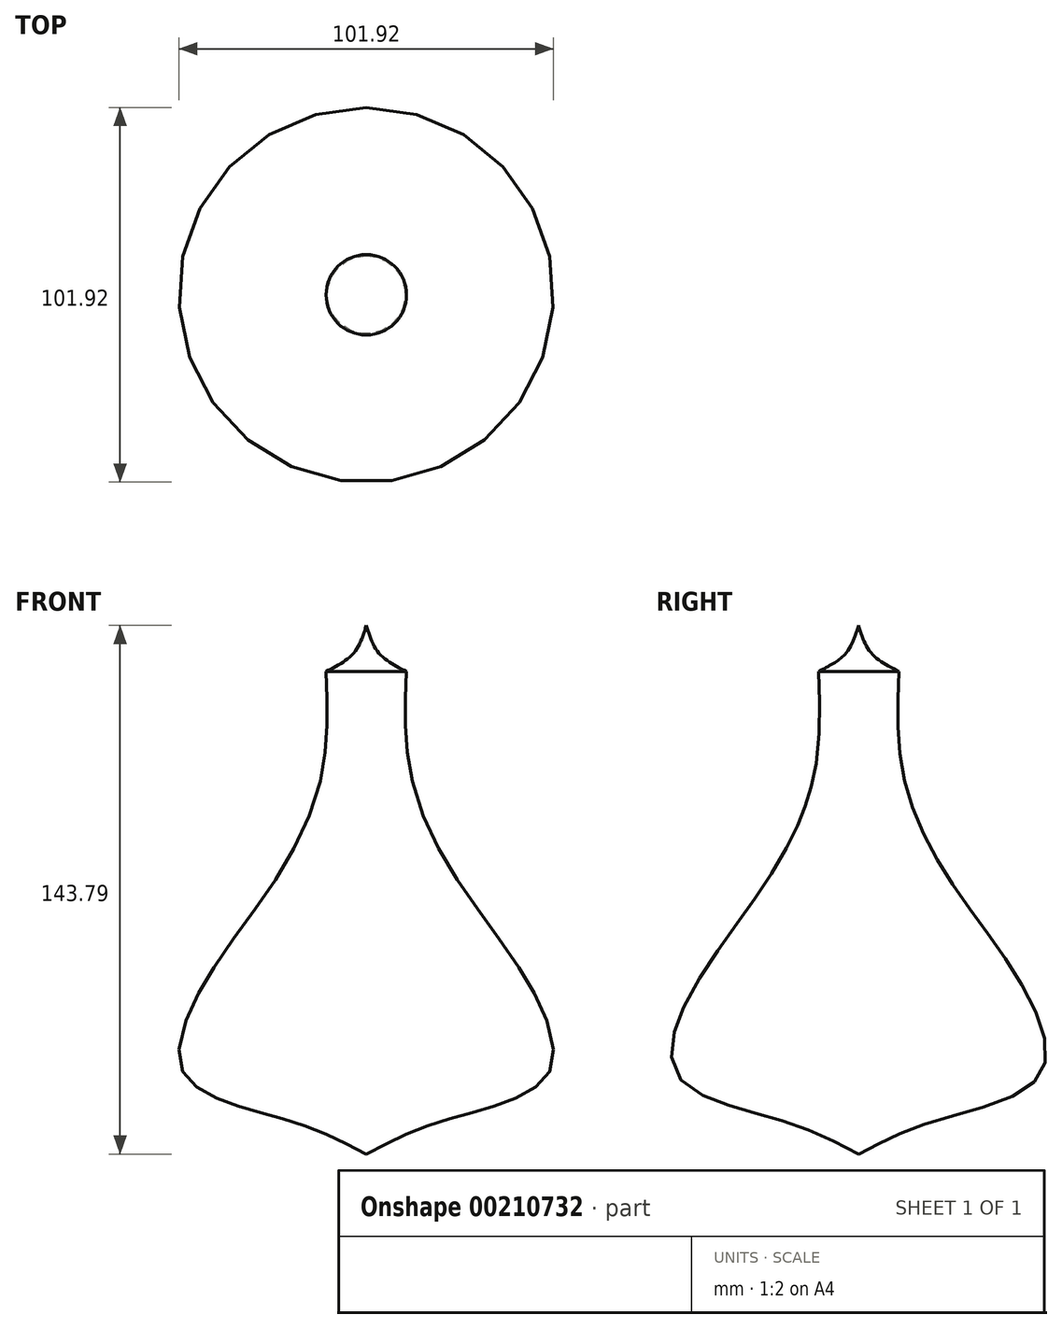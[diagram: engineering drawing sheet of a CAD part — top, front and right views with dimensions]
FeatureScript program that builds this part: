
annotation { "Feature Type Name" : "Feature", "Feature Type Description" : "" }
export const myFeature = defineFeature(function(context is Context, id is Id, definition is map)
    precondition{}
    {
        {
            var Q0;
            Q0=qCreatedBy(makeId("Right.planeOp"),FACE);
            var sketch = newSketch(context, id + "F0", { "sketchPlane" : qUnion([Q0])});
            skFitSpline(sketch, "E0", {"points": [v(10.94, 61.42) * mm, v(12.2, 32.98) * mm, v(24.7, 4.85) * mm, v(44.39, -23.91) * mm, v(49.39, -48.3) * mm, v(20.94, -60.8) * mm, v(0, -69.86) * mm], "startDerivative": vector(-6.65, -172.6) * mm, "endDerivative": vector(-122.75, -64.17) * mm});
            skFitSpline(sketch, "E1", {"points": [v(10.94, 61.42) * mm, v(3.44, 66.42) * mm, v(0, 73.93) * mm], "startDerivative": vector(-16.63, 8.37) * mm, "endDerivative": vector(-5.16, 16.7) * mm});
            skLineSegment(sketch, "E2", {"start": v(0, 79.55) * mm, "end": v(0, 98) * mm});
            skSolve(sketch);
        }
        {
            var Q0;
            Q0=sQuery(id+"F0.wireOp",EDGE,"E0");
            var Q1;
            Q1=sQuery(id+"F0.wireOp",EDGE,"E1");
            var Q2;
            Q2=sQuery(id+"F0.wireOp",EDGE,"E2");
            revolve(context, id + "F1", {"bodyType" : ToolBodyType.SURFACE, "surfaceEntities" : qUnion([Q0, Q1]), "axis" : qUnion([Q2]), "revolveType" : RevolveType.FULL});
        }
    });
